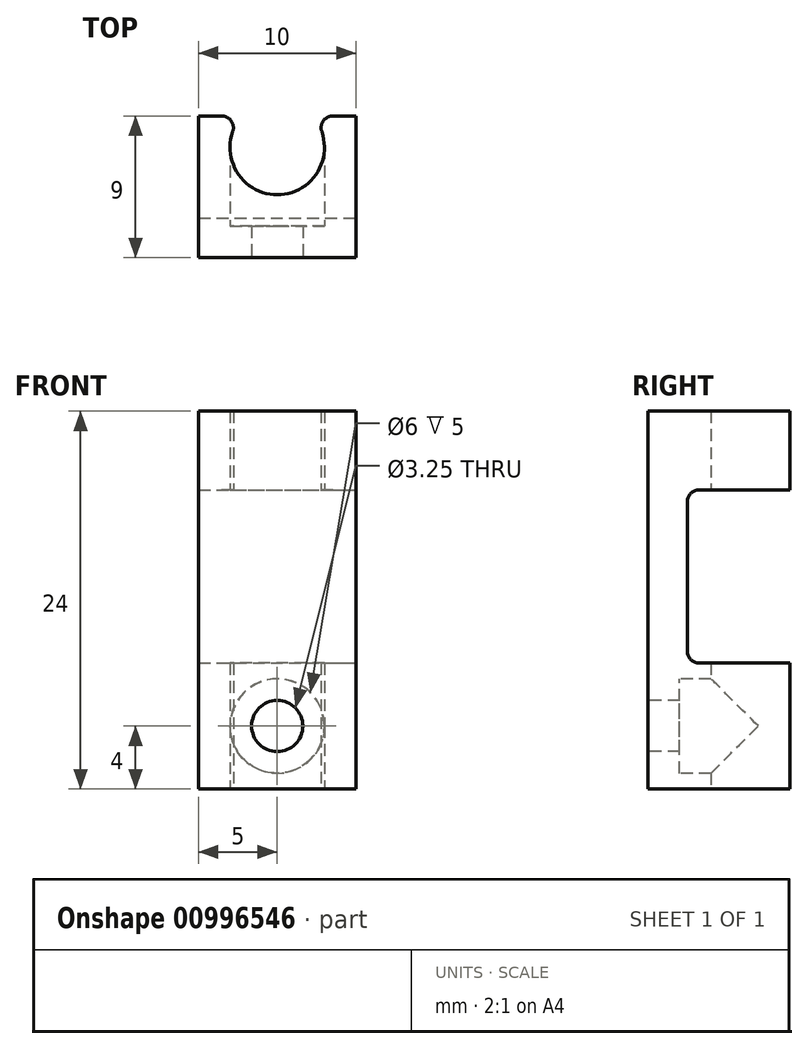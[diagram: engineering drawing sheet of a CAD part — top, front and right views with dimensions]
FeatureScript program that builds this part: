
annotation { "Feature Type Name" : "Feature", "Feature Type Description" : "" }
export const myFeature = defineFeature(function(context is Context, id is Id, definition is map)
    precondition{}
    {
        {
            var Q0;
            Q0=qCreatedBy(makeId("Top.planeOp"),FACE);
            var sketch = newSketch(context, id + "F0", { "sketchPlane" : qUnion([Q0])});
            skLineSegment(sketch, "E0", {"start": v(0, 0) * mm, "end": v(12, 0) * mm});
            skLineSegment(sketch, "E1", {"start": v(12, 9) * mm, "end": v(12, 0) * mm});
            skLineSegment(sketch, "E2", {"start": v(0, 9) * mm, "end": v(0, 0) * mm});
            skArc(sketch, "E3", {"start": v(3.76, 9) * mm, "mid": v(6, 4) * mm, "end": v(8.24, 9) * mm});
            skLineSegment(sketch, "E4", {"start": v(0, 9) * mm, "end": v(3.76, 9) * mm});
            skLineSegment(sketch, "E5", {"start": v(8.24, 9) * mm, "end": v(12, 9) * mm});
            skSolve(sketch);
        }
        {
            var Q0;
            Q0=makeQuery(id+"F0.imprint","IMPRINT",FACE,{"disambiguationData":[TD([[makeQuery(id+"F0.imprint","IMPRINT",EDGE,{"derivedFrom":sQuery(id+"F0.wireOp",EDGE,"E0")}),1.0]])]});
            extrude(context, id + "F1", {"entities" : qUnion([Q0]), "depth" : 25 * mm, "offsetDistance" : 25 * mm});
        }
        {
            var Q0;
            Q0=makeQuery(id+"F1.opExtrude","SWEPT_FACE",FACE,{"disambiguationData":[OSD([sQuery(id+"F0.wireOp",EDGE,"E2")])]});
            extrude(context, id + "F2", {"entities" : qUnion([Q0]), "operationType" : NewBodyOperationType.REMOVE, "oppositeDirection" : true, "depth" : 1 * mm, "offsetDistance" : 25 * mm});
        }
        {
            var Q0;
            Q0=makeQuery(id+"F1.opExtrude","SWEPT_FACE",FACE,{"disambiguationData":[OSD([sQuery(id+"F0.wireOp",EDGE,"E1")])]});
            extrude(context, id + "F3", {"entities" : qUnion([Q0]), "operationType" : NewBodyOperationType.REMOVE, "oppositeDirection" : true, "depth" : 1 * mm, "offsetDistance" : 25 * mm});
        }
        {
            var Q0;
            Q0=makeQuery(id+"F3.boolean.opBoolean","COPY",FACE,{"derivedFrom":makeQuery(id+"F3.opExtrude","CAP_FACE",FACE,{"disambiguationData":[OSD([sQuery(id+"F0.wireOp",EDGE,"E1")])],"isStart":false})});
            var sketch = newSketch(context, id + "F4", { "sketchPlane" : qUnion([Q0])});
            skLineSegment(sketch, "E6", {"start": v(9, 25) * mm, "end": v(9, 20) * mm});
            skLineSegment(sketch, "E7", {"start": v(9, 20) * mm, "end": v(9, 9) * mm});
            skLineSegment(sketch, "E8", {"start": v(9, 9) * mm, "end": v(9, 5) * mm});
            skLineSegment(sketch, "E9", {"start": v(9, 5) * mm, "end": v(9, 1) * mm});
            skLineSegment(sketch, "E10", {"start": v(9, 20) * mm, "end": v(3, 20) * mm});
            skLineSegment(sketch, "E11", {"start": v(3, 20) * mm, "end": v(3, 9) * mm});
            skLineSegment(sketch, "E12", {"start": v(3, 9) * mm, "end": v(9, 9) * mm});
            skLineSegment(sketch, "E13", {"start": v(9, 1) * mm, "end": v(3, 1) * mm});
            skLineSegment(sketch, "E14", {"start": v(3, 1) * mm, "end": v(3, 0) * mm});
            skSolve(sketch);
        }
        {
            var Q0;
            Q0=makeQuery(id+"F4.imprint","IMPRINT",FACE,{"disambiguationData":[TD([[makeQuery(id+"F4.imprint","IMPRINT",EDGE,{"derivedFrom":sQuery(id+"F4.wireOp",EDGE,"E7")}),-1.0]])]});
            var Q1;
            {var subQ0=sQuery(id+"F4.wireOp",EDGE,"E13");Q1=makeQuery(id+"F4.imprint","IMPRINT",FACE,{"disambiguationData":[TD([[makeQuery(id+"F4.imprint","IMPRINT",EDGE,{"derivedFrom":subQ0}),1.0]])]});}
            extrude(context, id + "F5", {"entities" : qUnion([Q0, Q1]), "operationType" : NewBodyOperationType.REMOVE, "oppositeDirection" : true, "depth" : 25 * mm, "offsetDistance" : 25 * mm});
        }
        {
            var Q0;
            Q0=makeQuery(id+"F1.opExtrude","SWEPT_FACE",FACE,{"disambiguationData":[OSD([sQuery(id+"F0.wireOp",EDGE,"E0")])]});
            var sketch = newSketch(context, id + "F6", { "sketchPlane" : qUnion([Q0])});
            skPoint(sketch, "E15.endSnap0", {"position": v(6, 0) * mm});
            skCircle(sketch, "E16", {"center": v(6, 5) * mm, "radius": 3 * mm});
            skCircle(sketch, "E17", {"center": v(6, 5) * mm, "radius": 1.63 * mm});
            skSolve(sketch);
        }
        {
            var Q0;
            Q0=makeQuery(id+"F6.imprint","IMPRINT",FACE,{"disambiguationData":[TD([[makeQuery(id+"F6.imprint","IMPRINT",EDGE,{"derivedFrom":sQuery(id+"F6.wireOp",EDGE,"E16")}),1.0]])]});
            var Q1;
            Q1=makeQuery(id+"F6.imprint","IMPRINT",FACE,{"disambiguationData":[TD([[makeQuery(id+"F6.imprint","IMPRINT",EDGE,{"derivedFrom":sQuery(id+"F6.wireOp",EDGE,"E17")}),1.0]])]});
            extrude(context, id + "F7", {"entities" : qUnion([Q0, Q1]), "operationType" : NewBodyOperationType.REMOVE, "oppositeDirection" : true, "depth" : 7 * mm, "offsetDistance" : 25 * mm});
        }
        {
            var Q0;
            Q0=makeQuery(id+"F6.imprint","IMPRINT",FACE,{"disambiguationData":[TD([[makeQuery(id+"F6.imprint","IMPRINT",EDGE,{"derivedFrom":sQuery(id+"F6.wireOp",EDGE,"E16")}),1.0]])]});
            extrude(context, id + "F8", {"entities" : qUnion([Q0]), "operationType" : NewBodyOperationType.ADD, "oppositeDirection" : true, "depth" : 2 * mm, "offsetDistance" : 25 * mm});
        }
        {
            var Q0;
            Q0=makeQuery(id+"F1.opExtrude","CAP_FACE",FACE,{"disambiguationData":[OSD([sQuery(id+"F0.wireOp",EDGE,"E0"),sQuery(id+"F0.wireOp",EDGE,"E1"),sQuery(id+"F0.wireOp",EDGE,"E2"),sQuery(id+"F0.wireOp",EDGE,"E3"),sQuery(id+"F0.wireOp",EDGE,"E4"),sQuery(id+"F0.wireOp",EDGE,"E5")])],"isStart":true});
            extrude(context, id + "F9", {"entities" : qUnion([Q0]), "operationType" : NewBodyOperationType.REMOVE, "oppositeDirection" : true, "depth" : 1 * mm, "offsetDistance" : 25 * mm});
        }
        {
            var Q0;
            {var subQ0=sQuery(id+"F0.wireOp",EDGE,"E3");var subQ1=sQuery(id+"F0.wireOp",EDGE,"E5");Q0=makeQuery(id+"F5.boolean.opBoolean","SPLIT",EDGE,{"disambiguationData":[TD([makeQuery(id+"F5.opExtrude","SWEPT_FACE",FACE,{"disambiguationData":[OSD([sQuery(id+"F4.wireOp",EDGE,"E12")])]})])],"derivedFrom":makeQuery(id+"F1.opExtrude","SWEPT_EDGE",EDGE,{"disambiguationData":[OSD([subQ0,subQ1])]})});}
            var Q1;
            {var subQ0=sQuery(id+"F0.wireOp",EDGE,"E3");var subQ1=sQuery(id+"F0.wireOp",EDGE,"E4");Q1=makeQuery(id+"F5.boolean.opBoolean","SPLIT",EDGE,{"disambiguationData":[TD([makeQuery(id+"F5.opExtrude","SWEPT_FACE",FACE,{"disambiguationData":[OSD([sQuery(id+"F4.wireOp",EDGE,"E12")])]})])],"derivedFrom":makeQuery(id+"F1.opExtrude","SWEPT_EDGE",EDGE,{"disambiguationData":[OSD([subQ0,subQ1])]})});}
            var Q2;
            {var subQ0=sQuery(id+"F0.wireOp",EDGE,"E4");var subQ1=sQuery(id+"F0.wireOp",EDGE,"E3");Q2=makeQuery(id+"F5.boolean.opBoolean","SPLIT",EDGE,{"disambiguationData":[TD([makeQuery(id+"F5.opExtrude","SWEPT_FACE",FACE,{"disambiguationData":[OSD([sQuery(id+"F4.wireOp",EDGE,"E10")])]})])],"derivedFrom":makeQuery(id+"F1.opExtrude","SWEPT_EDGE",EDGE,{"disambiguationData":[OSD([subQ1,subQ0])]})});}
            var Q3;
            {var subQ0=sQuery(id+"F0.wireOp",EDGE,"E5");var subQ1=sQuery(id+"F0.wireOp",EDGE,"E3");Q3=makeQuery(id+"F5.boolean.opBoolean","SPLIT",EDGE,{"disambiguationData":[TD([makeQuery(id+"F5.opExtrude","SWEPT_FACE",FACE,{"disambiguationData":[OSD([sQuery(id+"F4.wireOp",EDGE,"E10")])]})])],"derivedFrom":makeQuery(id+"F1.opExtrude","SWEPT_EDGE",EDGE,{"disambiguationData":[OSD([subQ1,subQ0])]})});}
            fillet(context, id + "F10", {"entities" : qUnion([Q0, Q1, Q2, Q3]), "radius" : .75 * mm, "tangentPropagation" : true, "allowEdgeOverflow" : false});
        }
        {
            var Q0;
            Q0=makeQuery(id+"F5.boolean.opBoolean","COPY",FACE,{"derivedFrom":makeQuery(id+"F5.opExtrude","SWEPT_FACE",FACE,{"disambiguationData":[OSD([sQuery(id+"F4.wireOp",EDGE,"E11")])]})});
            extrude(context, id + "F11", {"entities" : qUnion([Q0]), "operationType" : NewBodyOperationType.REMOVE, "oppositeDirection" : true, "depth" : .5 * mm, "offsetDistance" : 25 * mm});
        }
        {
            var Q0;
            Q0=makeQuery(id+"F11.boolean.opBoolean","COPY",EDGE,{"derivedFrom":makeQuery(id+"F11.opExtrude","CAP_EDGE",EDGE,{"disambiguationData":[OSD([sQuery(id+"F4.wireOp",EDGE,"E11")])],"isStart":false})});
            var Q1;
            Q1=makeQuery(id+"F11.boolean.opBoolean","COPY",EDGE,{"derivedFrom":makeQuery(id+"F11.opExtrude","CAP_EDGE",EDGE,{"disambiguationData":[OSD([sQuery(id+"F0.wireOp",EDGE,"E2"),sQuery(id+"F4.wireOp",EDGE,"E11")])],"isStart":false})});
            fillet(context, id + "F12", {"entities" : qUnion([Q0, Q1]), "radius" : .75 * mm, "tangentPropagation" : true, "allowEdgeOverflow" : false});
        }
    });
